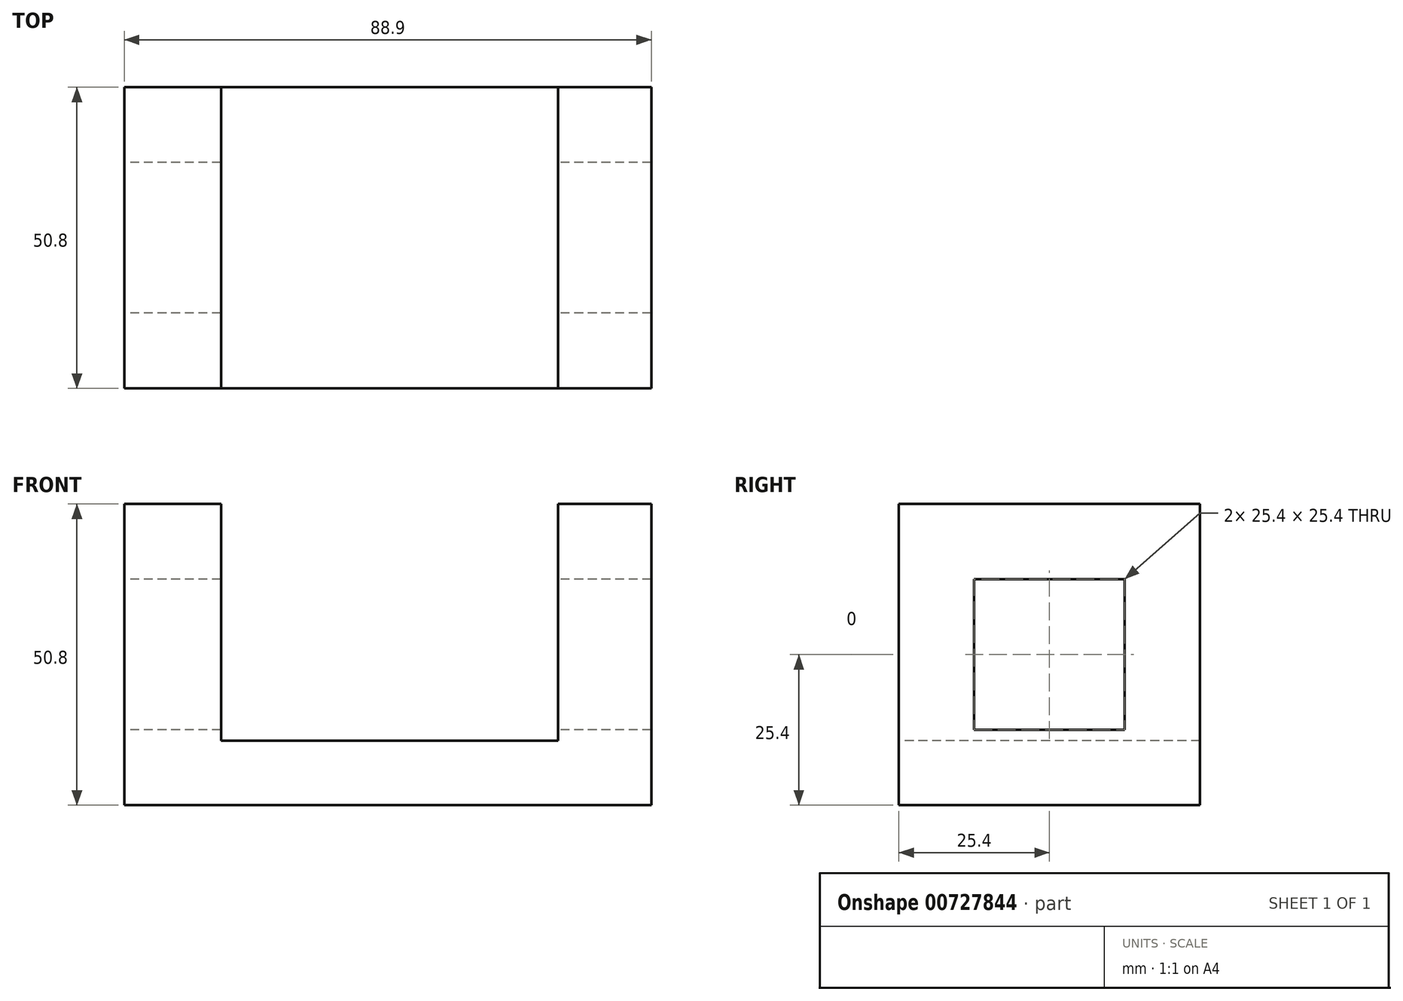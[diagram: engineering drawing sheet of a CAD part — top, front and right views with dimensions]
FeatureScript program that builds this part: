
annotation { "Feature Type Name" : "Feature", "Feature Type Description" : "" }
export const myFeature = defineFeature(function(context is Context, id is Id, definition is map)
    precondition{}
    {
        {
            var Q0;
            Q0=qCreatedBy(makeId("Right.planeOp"),FACE);
            var sketch = newSketch(context, id + "F0", { "sketchPlane" : qUnion([Q0])});
            skLineSegment(sketch, "E0.bottom", {"start": v(-27.6, 25.4) * mm, "end": v(23.2, 25.4) * mm});
            skLineSegment(sketch, "E0.top", {"start": v(-27.6, -25.4) * mm, "end": v(23.2, -25.4) * mm});
            skLineSegment(sketch, "E0.left", {"start": v(-27.6, 25.4) * mm, "end": v(-27.6, -25.4) * mm});
            skLineSegment(sketch, "E0.right", {"start": v(23.2, 25.4) * mm, "end": v(23.2, -25.4) * mm});
            skPoint(sketch, "E0.middle", {"position": v(-2.2, 0) * mm});
            skLineSegment(sketch, "E1.bottom", {"start": v(-14.9, 12.7) * mm, "end": v(10.5, 12.7) * mm});
            skLineSegment(sketch, "E1.top", {"start": v(-14.9, -12.7) * mm, "end": v(10.5, -12.7) * mm});
            skLineSegment(sketch, "E1.left", {"start": v(-14.9, 12.7) * mm, "end": v(-14.9, -12.7) * mm});
            skLineSegment(sketch, "E1.right", {"start": v(10.5, 12.7) * mm, "end": v(10.5, -12.7) * mm});
            skSolve(sketch);
        }
        {
            var Q0;
            Q0=makeQuery(id+"F0.imprint","IMPRINT",FACE,{"disambiguationData":[TD([[makeQuery(id+"F0.imprint","IMPRINT",EDGE,{"derivedFrom":sQuery(id+"F0.wireOp",EDGE,"E0.bottom")}),-1.0]])]});
            extrude(context, id + "F1", {"entities" : qUnion([Q0]), "depth" : 88.9 * mm, "offsetDistance" : 25.4 * mm});
        }
        {
            var Q0;
            Q0=makeQuery(id+"F1.opExtrude","SWEPT_FACE",FACE,{"disambiguationData":[OSD([sQuery(id+"F0.wireOp",EDGE,"E0.left")])]});
            var sketch = newSketch(context, id + "F2", { "sketchPlane" : qUnion([Q0])});
            skLineSegment(sketch, "E2.bottom", {"start": v(16.31, 25.4) * mm, "end": v(73.19, 25.4) * mm});
            skLineSegment(sketch, "E2.top", {"start": v(16.31, -14.55) * mm, "end": v(73.19, -14.55) * mm});
            skLineSegment(sketch, "E2.left", {"start": v(16.31, 25.4) * mm, "end": v(16.31, -14.55) * mm});
            skLineSegment(sketch, "E2.right", {"start": v(73.19, 25.4) * mm, "end": v(73.19, -14.55) * mm});
            skSolve(sketch);
        }
        {
            var Q0;
            Q0=makeQuery(id+"F2.imprint","IMPRINT",FACE,{"disambiguationData":[TD([[makeQuery(id+"F2.imprint","IMPRINT",EDGE,{"derivedFrom":sQuery(id+"F2.wireOp",EDGE,"E2.bottom")}),1.0]])]});
            extrude(context, id + "F3", {"entities" : qUnion([Q0]), "operationType" : NewBodyOperationType.REMOVE, "oppositeDirection" : true, "depth" : 50.8 * mm, "offsetDistance" : 25.4 * mm});
        }
    });
